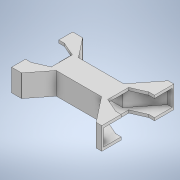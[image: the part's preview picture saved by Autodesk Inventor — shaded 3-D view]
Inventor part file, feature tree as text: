
AUTODESK INVENTOR PART (.ipt)
format: ipt  version: 2022 (Build 260153000, 153)  size: 240,640 bytes
history: native  units: mm
features: extrude x6, sketch x6
ambient origin geometry x8: Origin, YZ Plane, XZ Plane, XY Plane, X Axis, Y Axis, Z Axis, Center Point
bodies: Solid1 (feature_tree)
feature tree (12):
  extrude  "Extrusion1"  Depth=65.0mm
  extrude  "Extrusion2"  Depth=10.0mm
  extrude  "Extrusion3"  Depth=3.0mm
  extrude  "Extrusion4"  Depth=5.0mm TaperAngle=0.0deg
  extrude  "Extrusion5"  Depth=30.0mm
  extrude  "Extrusion6"  Depth=35.4mm
  sketch  "Sketch1"  dims[d0=172.412mm d1=65.0mm]
  sketch  "Sketch2"  dims[d2=65.0mm d7=10.0mm]
  sketch  "Sketch3"  dims[d8=5.0mm d9=0.0mm d10=3.0mm]
  sketch  "Sketch4"  dims[d11=30.0mm d12=0.0mm d13=5.0mm d14=0.0mm]
  sketch  "Sketch5"  dims[d15=30.0mm d16=30.0mm]
  sketch  "Sketch6"  dims[d17=10.0mm d18=35.4mm d19=18.85mm d20=18.85mm d21=0.0mm d22=0.0mm d23=10.0mm d24=10.0mm d25=0.0mm d26=0.0mm d27=3.0mm d28=3.0mm d29=18.0mm d30=0.0mm]
